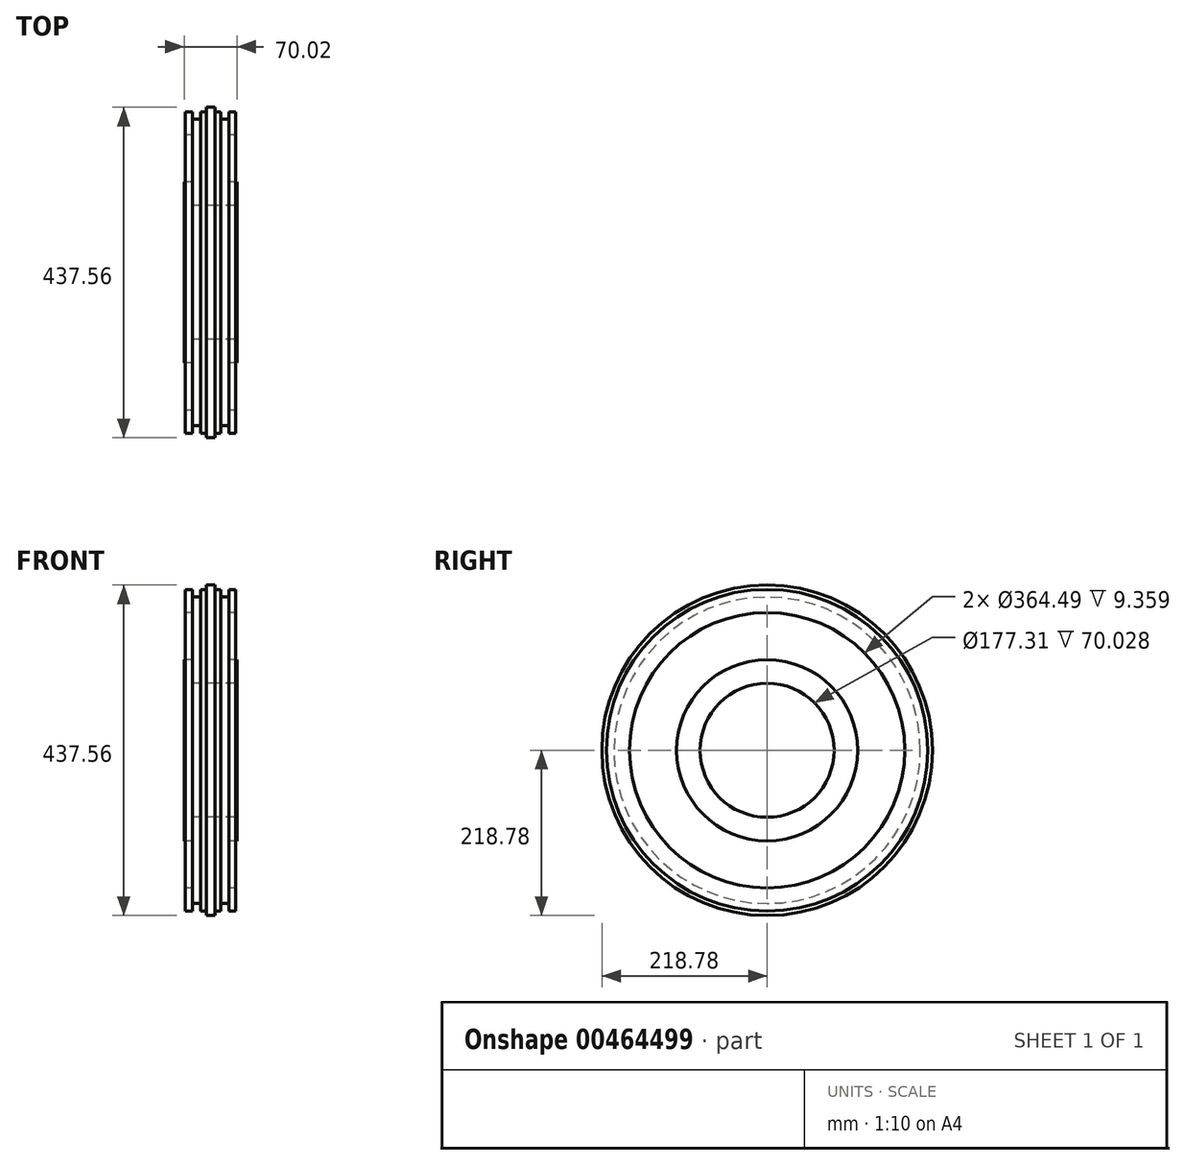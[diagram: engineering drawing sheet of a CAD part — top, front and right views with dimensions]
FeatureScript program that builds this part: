
annotation { "Feature Type Name" : "Feature", "Feature Type Description" : "" }
export const myFeature = defineFeature(function(context is Context, id is Id, definition is map)
    precondition{}
    {
        {
            var Q0;
            Q0=qCreatedBy(makeId("Front.planeOp"),FACE);
            var sketch = newSketch(context, id + "F0", { "sketchPlane" : qUnion([Q0])});
            skLineSegment(sketch, "E0", {"start": v(0, 74.74) * mm, "end": v(0, -75) * mm, "construction": true});
            skLineSegment(sketch, "E1", {"start": v(0, 64.44) * mm, "end": v(-35.01, 64.44) * mm});
            skLineSegment(sketch, "E2", {"start": v(-35.01, 64.44) * mm, "end": v(-35.01, 33.25) * mm});
            skLineSegment(sketch, "E3", {"start": v(-35.01, 33.25) * mm, "end": v(-24.1, 33.25) * mm});
            skLineSegment(sketch, "E4", {"start": v(-24.1, 33.25) * mm, "end": v(-24.1, -29.14) * mm});
            skLineSegment(sketch, "E5", {"start": v(-24.1, -29.14) * mm, "end": v(-33.45, -29.14) * mm});
            skLineSegment(sketch, "E6", {"start": v(-33.45, -29.14) * mm, "end": v(-33.45, -59.72) * mm});
            skLineSegment(sketch, "E7", {"start": v(-33.45, -59.72) * mm, "end": v(-24.1, -59.72) * mm});
            skLineSegment(sketch, "E8", {"start": v(-24.1, -59.72) * mm, "end": v(-24.1, -49.73) * mm});
            skLineSegment(sketch, "E9", {"start": v(-24.1, -49.73) * mm, "end": v(-13.49, -49.73) * mm});
            skLineSegment(sketch, "E10", {"start": v(-13.49, -49.73) * mm, "end": v(-13.49, -59.72) * mm});
            skLineSegment(sketch, "E11", {"start": v(-13.49, -59.72) * mm, "end": v(-5.69, -59.72) * mm});
            skLineSegment(sketch, "E12", {"start": v(-5.69, -59.72) * mm, "end": v(-5.69, -65.68) * mm});
            skLineSegment(sketch, "E13", {"start": v(-5.69, -65.68) * mm, "end": v(0, -65.68) * mm});
            skLineSegment(sketch, "E14.MirrorCS", {"start": v(0, 64.44) * mm, "end": v(35.01, 64.44) * mm});
            skLineSegment(sketch, "E15.MirrorCS", {"start": v(35.01, 64.44) * mm, "end": v(35.01, 33.25) * mm});
            skLineSegment(sketch, "E16.MirrorCS", {"start": v(35.01, 33.25) * mm, "end": v(24.1, 33.25) * mm});
            skLineSegment(sketch, "E17.MirrorCS", {"start": v(24.1, 33.25) * mm, "end": v(24.1, -29.14) * mm});
            skLineSegment(sketch, "E18.MirrorCS", {"start": v(24.1, -29.14) * mm, "end": v(33.45, -29.14) * mm});
            skLineSegment(sketch, "E19.MirrorCS", {"start": v(33.45, -29.14) * mm, "end": v(33.45, -59.72) * mm});
            skLineSegment(sketch, "E20.MirrorCS", {"start": v(33.45, -59.72) * mm, "end": v(24.1, -59.72) * mm});
            skLineSegment(sketch, "E21.MirrorCS", {"start": v(24.1, -49.73) * mm, "end": v(13.49, -49.73) * mm});
            skLineSegment(sketch, "E22.MirrorCS", {"start": v(13.49, -49.73) * mm, "end": v(13.49, -59.72) * mm});
            skLineSegment(sketch, "E23.MirrorCS", {"start": v(13.49, -59.72) * mm, "end": v(5.69, -59.72) * mm});
            skLineSegment(sketch, "E24.MirrorCS", {"start": v(5.69, -65.68) * mm, "end": v(0, -65.68) * mm});
            skLineSegment(sketch, "E25.MirrorCS", {"start": v(5.69, -59.72) * mm, "end": v(5.69, -65.68) * mm});
            skLineSegment(sketch, "E26.MirrorCS", {"start": v(24.1, -59.72) * mm, "end": v(24.1, -49.73) * mm});
            skLineSegment(sketch, "E27", {"start": v(-131.35, 153.1) * mm, "end": v(133.36, 153.1) * mm, "construction": true});
            skSolve(sketch);
        }
        {
            var Q0;
            Q0=makeQuery(id+"F0.imprint","IMPRINT",FACE,{"disambiguationData":[TD([[makeQuery(id+"F0.imprint","IMPRINT",EDGE,{"derivedFrom":sQuery(id+"F0.wireOp",EDGE,"E1")}),1.0]])]});
            var Q1;
            Q1=sQuery(id+"F0.wireOp",EDGE,"E27");
            revolve(context, id + "F1", {"entities" : qUnion([Q0]), "axis" : qUnion([Q1]), "revolveType" : RevolveType.FULL});
        }
    });
